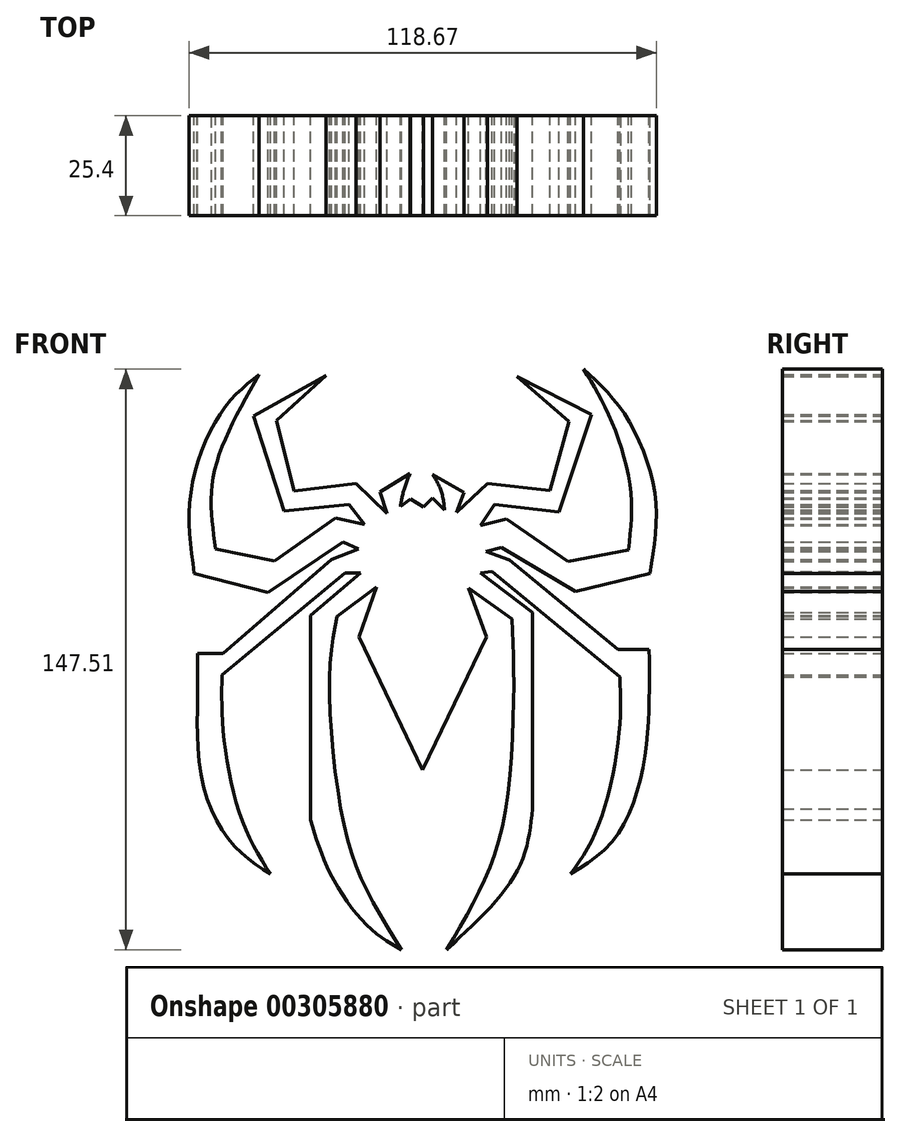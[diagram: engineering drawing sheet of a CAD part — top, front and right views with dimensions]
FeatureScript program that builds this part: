
annotation { "Feature Type Name" : "Feature", "Feature Type Description" : "" }
export const myFeature = defineFeature(function(context is Context, id is Id, definition is map)
    precondition{}
    {
        {
            var Q0;
            Q0=qCreatedBy(makeId("Front.planeOp"),FACE);
            var sketch = newSketch(context, id + "F0", { "sketchPlane" : qUnion([Q0])});
            skLineSegment(sketch, "E0", {"start": v(-26.37, 19.63) * mm, "end": v(-30.8, 6.94) * mm});
            skLineSegment(sketch, "E1", {"start": v(-30.8, 6.94) * mm, "end": v(-14.7, -26.87) * mm});
            skLineSegment(sketch, "E2", {"start": v(-14.7, -26.87) * mm, "end": v(1.61, 6.94) * mm});
            skLineSegment(sketch, "E3", {"start": v(1.61, 6.94) * mm, "end": v(-3.02, 19.42) * mm});
            skLineSegment(sketch, "E4", {"start": v(-3.02, 19.42) * mm, "end": v(8.05, 11.57) * mm});
            skLineSegment(sketch, "E5", {"start": v(-26.37, 19.63) * mm, "end": v(-36.43, 12.18) * mm});
            skLineSegment(sketch, "E6", {"start": v(-30.4, 23.25) * mm, "end": v(-43.07, 12.38) * mm});
            skLineSegment(sketch, "E7", {"start": v(-43.07, 12.38) * mm, "end": v(-43.07, -39.55) * mm});
            skLineSegment(sketch, "E8", {"start": v(0, 23.25) * mm, "end": v(13.28, 13.18) * mm});
            skPoint(sketch, "E8.endSnap0", {"position": v(-0.7, 13.18) * mm});
            skLineSegment(sketch, "E9", {"start": v(13.28, 13.18) * mm, "end": v(13.28, -36.73) * mm});
            skLineSegment(sketch, "E10", {"start": v(-39.25, 73.37) * mm, "end": v(-57.57, 63.1) * mm});
            skLineSegment(sketch, "E11", {"start": v(-57.57, 63.1) * mm, "end": v(-49.92, 38.95) * mm});
            skLineSegment(sketch, "E12", {"start": v(-49.92, 38.95) * mm, "end": v(-33.41, 40.56) * mm});
            skLineSegment(sketch, "E13", {"start": v(-33.41, 40.56) * mm, "end": v(-29.39, 35.53) * mm});
            skLineSegment(sketch, "E14", {"start": v(-29.39, 35.53) * mm, "end": v(-36.83, 37.14) * mm});
            skLineSegment(sketch, "E15", {"start": v(-36.83, 37.14) * mm, "end": v(-52.33, 26.27) * mm});
            skLineSegment(sketch, "E16", {"start": v(-52.33, 26.27) * mm, "end": v(-67.23, 29.29) * mm});
            skLineSegment(sketch, "E17", {"start": v(-23.75, 38.34) * mm, "end": v(-31.6, 46) * mm});
            skLineSegment(sketch, "E18", {"start": v(-31.6, 46) * mm, "end": v(-47.3, 43.98) * mm});
            skLineSegment(sketch, "E19", {"start": v(-47.3, 43.98) * mm, "end": v(-51.73, 61.9) * mm});
            skLineSegment(sketch, "E20", {"start": v(-51.73, 61.9) * mm, "end": v(-39.25, 73.37) * mm});
            skLineSegment(sketch, "E21", {"start": v(-6.04, 38.55) * mm, "end": v(1.81, 46) * mm});
            skLineSegment(sketch, "E22", {"start": v(1.81, 46) * mm, "end": v(17.71, 44.18) * mm});
            skLineSegment(sketch, "E23", {"start": v(17.71, 44.18) * mm, "end": v(22.54, 61.7) * mm});
            skLineSegment(sketch, "E24", {"start": v(22.54, 61.7) * mm, "end": v(9.26, 73.17) * mm});
            skLineSegment(sketch, "E25", {"start": v(9.26, 73.17) * mm, "end": v(28.18, 63.5) * mm});
            skLineSegment(sketch, "E26", {"start": v(28.18, 63.5) * mm, "end": v(19.93, 38.75) * mm});
            skLineSegment(sketch, "E27", {"start": v(19.93, 38.75) * mm, "end": v(3.62, 40.56) * mm});
            skLineSegment(sketch, "E28", {"start": v(3.62, 40.56) * mm, "end": v(0, 35.33) * mm});
            skLineSegment(sketch, "E29", {"start": v(0, 35.33) * mm, "end": v(6.64, 36.94) * mm});
            skLineSegment(sketch, "E30", {"start": v(6.64, 36.94) * mm, "end": v(22.26, 26.12) * mm});
            skLineSegment(sketch, "E31", {"start": v(22.26, 26.12) * mm, "end": v(37.64, 29.09) * mm});
            skLineSegment(sketch, "E32", {"start": v(1.4, 28.68) * mm, "end": v(7.45, 26.47) * mm});
            skLineSegment(sketch, "E33", {"start": v(7.45, 26.47) * mm, "end": v(35.02, 3.72) * mm});
            skLineSegment(sketch, "E34", {"start": v(35.02, 3.72) * mm, "end": v(42.87, 3.72) * mm});
            skLineSegment(sketch, "E35", {"start": v(-31, 29.29) * mm, "end": v(-34.82, 31.1) * mm});
            skLineSegment(sketch, "E36", {"start": v(-34.82, 31.1) * mm, "end": v(-53.94, 18.22) * mm});
            skLineSegment(sketch, "E37", {"start": v(-53.94, 18.22) * mm, "end": v(-72.66, 23.05) * mm});
            skLineSegment(sketch, "E38", {"start": v(-31, 29.29) * mm, "end": v(-37.84, 26.67) * mm});
            skLineSegment(sketch, "E39", {"start": v(-37.84, 26.67) * mm, "end": v(-65.42, 2.72) * mm});
            skLineSegment(sketch, "E40", {"start": v(-65.42, 2.72) * mm, "end": v(-71.86, 2.72) * mm});
            skLineSegment(sketch, "E41", {"start": v(-30.4, 23.25) * mm, "end": v(-34.42, 23.25) * mm});
            skPoint(sketch, "E41.endSnap0", {"position": v(-34.42, 27.98) * mm});
            skLineSegment(sketch, "E42", {"start": v(-34.42, 23.25) * mm, "end": v(-65.62, -2.72) * mm});
            skLineSegment(sketch, "E43", {"start": v(0, 23.25) * mm, "end": v(3.01, 23.54) * mm});
            skLineSegment(sketch, "E44", {"start": v(3.01, 23.54) * mm, "end": v(35.45, -3.21) * mm});
            skLineSegment(sketch, "E45", {"start": v(-20.33, 40.16) * mm, "end": v(-17.71, 41.97) * mm});
            skLineSegment(sketch, "E46", {"start": v(-17.71, 41.97) * mm, "end": v(-14.5, 39.95) * mm});
            skLineSegment(sketch, "E47", {"start": v(-14.5, 39.95) * mm, "end": v(-12.1, 42.27) * mm});
            skPoint(sketch, "E47.endSnap0", {"position": v(-2.11, 42.27) * mm});
            skLineSegment(sketch, "E48", {"start": v(-12.1, 42.27) * mm, "end": v(-9.1, 39.17) * mm});
            skLineSegment(sketch, "E49", {"start": v(-6.04, 38.55) * mm, "end": v(-4.2, 43.69) * mm});
            skLineSegment(sketch, "E50", {"start": v(-4.2, 43.69) * mm, "end": v(-12.1, 48.24) * mm});
            skLineSegment(sketch, "E51", {"start": v(-23.75, 38.34) * mm, "end": v(-25.46, 43.75) * mm});
            skLineSegment(sketch, "E52", {"start": v(-25.46, 43.75) * mm, "end": v(-17.85, 48.48) * mm});
            skFitSpline(sketch, "E53", {"points": [v(-17.85, 48.48) * mm, v(-19.52, 43.93) * mm, v(-20.33, 40.16) * mm], "startDerivative": vector(-3.56, -8.77) * mm, "endDerivative": vector(-1.36, -7.86) * mm});
            skFitSpline(sketch, "E54", {"points": [v(-12.1, 48.24) * mm, v(-9.95, 44.05) * mm, v(-9.1, 39.17) * mm], "startDerivative": vector(5.03, -8.2) * mm, "endDerivative": vector(1, -9.93) * mm});
            skLineSegment(sketch, "E55", {"start": v(1.4, 28.68) * mm, "end": v(5.4, 29.65) * mm});
            skLineSegment(sketch, "E56", {"start": v(5.4, 29.65) * mm, "end": v(24.2, 18.49) * mm});
            skLineSegment(sketch, "E57", {"start": v(24.2, 18.49) * mm, "end": v(43.1, 23.07) * mm});
            skFitSpline(sketch, "E58", {"points": [v(-56.2, 73.66) * mm, v(-67.71, 48.28) * mm, v(-67.23, 29.29) * mm], "startDerivative": vector(-27.06, -47.54) * mm, "endDerivative": vector(6.06, -41) * mm});
            skFitSpline(sketch, "E59", {"points": [v(-56.2, 73.66) * mm, v(-65.34, 64.7) * mm, v(-73.47, 44.21) * mm, v(-72.66, 23.05) * mm], "startDerivative": vector(-33.9, -26.88) * mm, "endDerivative": vector(8, -58.21) * mm});
            skFitSpline(sketch, "E60", {"points": [v(26.23, 74.98) * mm, v(32.49, 63.68) * mm, v(38.07, 44.9) * mm, v(37.64, 29.09) * mm], "startDerivative": vector(21.25, -34.33) * mm, "endDerivative": vector(-5.1, -45.94) * mm});
            skFitSpline(sketch, "E61", {"points": [v(26.23, 74.98) * mm, v(36.21, 64.19) * mm, v(44.34, 43.37) * mm, v(43.1, 23.07) * mm], "startDerivative": vector(35.23, -31.86) * mm, "endDerivative": vector(-9.56, -57.66) * mm});
            skFitSpline(sketch, "E62", {"points": [v(-71.86, 2.72) * mm, v(-71.86, -8.6) * mm, v(-70.42, -30.77) * mm, v(-62.3, -46.34) * mm, v(-53.33, -53.28) * mm], "startDerivative": vector(0.36, -47.3) * mm, "endDerivative": vector(42.9, -27.33) * mm});
            skFitSpline(sketch, "E63", {"points": [v(-53.33, -53.28) * mm, v(-60.77, -39.06) * mm, v(-65.34, -16.38) * mm, v(-65.62, -2.72) * mm], "startDerivative": vector(-25.3, 39.93) * mm, "endDerivative": vector(0.92, 42.3) * mm});
            skFitSpline(sketch, "E64", {"points": [v(42.87, 3.72) * mm, v(42.87, -9.75) * mm, v(41.04, -27.36) * mm, v(34.27, -44.11) * mm, v(22.93, -53.28) * mm], "startDerivative": vector(0.9, -56.67) * mm, "endDerivative": vector(-51.81, -32.44) * mm});
            skFitSpline(sketch, "E65", {"points": [v(22.93, -53.28) * mm, v(30.04, -40.9) * mm, v(35.29, -17.37) * mm, v(35.45, -3.21) * mm], "startDerivative": vector(24.96, 35.49) * mm, "endDerivative": vector(-1.81, 42.57) * mm});
            skFitSpline(sketch, "E66", {"points": [v(13.28, -36.73) * mm, v(9.4, -52.45) * mm, v(-8.54, -72.53) * mm], "startDerivative": vector(-3.9, -36.04) * mm, "endDerivative": vector(-38.3, -35.57) * mm});
            skFitSpline(sketch, "E67", {"points": [v(-8.54, -72.53) * mm, v(0, -57.1) * mm, v(6.16, -38.28) * mm, v(8.5, -6) * mm, v(8.05, 11.57) * mm], "startDerivative": vector(39.86, 67.54) * mm, "endDerivative": vector(-3.15, 69.64) * mm});
            skFitSpline(sketch, "E68", {"points": [v(-43.07, -39.55) * mm, v(-38.3, -52.8) * mm, v(-28.44, -66.61) * mm, v(-20.02, -72.53) * mm], "startDerivative": vector(11.06, -38.43) * mm, "endDerivative": vector(28.94, -16.6) * mm});
            skFitSpline(sketch, "E69", {"points": [v(-20.02, -72.53) * mm, v(-29.34, -56.4) * mm, v(-35.44, -36.73) * mm, v(-38.3, -2.77) * mm, v(-36.43, 12.18) * mm], "startDerivative": vector(-43.4, 68.95) * mm, "endDerivative": vector(12.16, 61.91) * mm});
            skSolve(sketch);
        }
        {
            var Q0;
            Q0=makeQuery(id+"F0.imprint","IMPRINT",FACE,{"disambiguationData":[TD([[makeQuery(id+"F0.imprint","IMPRINT",EDGE,{"derivedFrom":sQuery(id+"F0.wireOp",EDGE,"E0")}),1.0]])]});
            extrude(context, id + "F1", {"entities" : qUnion([Q0]), "depth" : 25.4 * mm});
        }
    });
